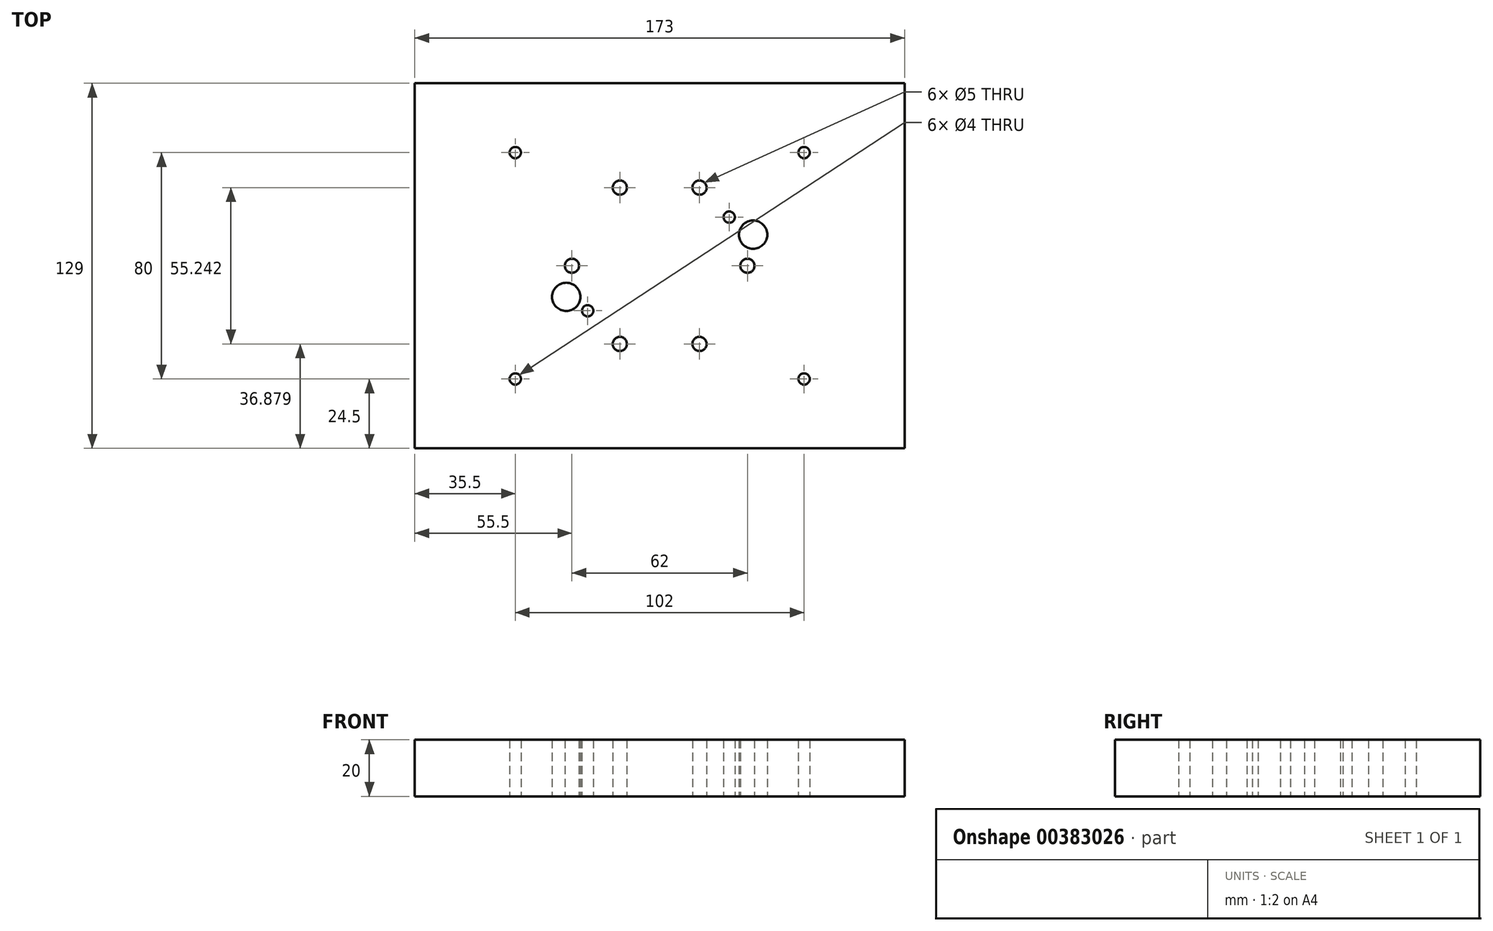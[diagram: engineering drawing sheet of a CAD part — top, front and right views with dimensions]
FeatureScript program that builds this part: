
annotation { "Feature Type Name" : "Feature", "Feature Type Description" : "" }
export const myFeature = defineFeature(function(context is Context, id is Id, definition is map)
    precondition{}
    {
        {
            var Q0;
            Q0=qCreatedBy(makeId("Top.planeOp"),FACE);
            var sketch = newSketch(context, id + "F0", { "sketchPlane" : qUnion([Q0])});
            skCircle(sketch, "E0", {"center": v(31, 0) * mm, "radius": 2.5 * mm});
            skCircle(sketch, "E1.1.0", {"center": v(14.07, 27.62) * mm, "radius": 2.5 * mm});
            skCircle(sketch, "E1.2.0", {"center": v(-14.07, 27.62) * mm, "radius": 2.5 * mm});
            skCircle(sketch, "E1.3.0", {"center": v(-31, 0) * mm, "radius": 2.5 * mm});
            skCircle(sketch, "E1.4.0", {"center": v(-14.07, -27.62) * mm, "radius": 2.5 * mm});
            skCircle(sketch, "E1.5.0", {"center": v(14.07, -27.62) * mm, "radius": 2.5 * mm});
            skPoint(sketch, "E1.center", {"position": v(0, 0) * mm});
            skLineSegment(sketch, "E2.bottom", {"start": v(-56, 45) * mm, "end": v(56, 45) * mm});
            skLineSegment(sketch, "E2.top", {"start": v(-56, -45) * mm, "end": v(56, -45) * mm});
            skLineSegment(sketch, "E2.left", {"start": v(-56, 45) * mm, "end": v(-56, -45) * mm});
            skLineSegment(sketch, "E2.right", {"start": v(56, 45) * mm, "end": v(56, -45) * mm});
            skLineSegment(sketch, "E3", {"start": v(-37.37, 11) * mm, "end": v(33, 11) * mm, "construction": true});
            skLineSegment(sketch, "E4", {"start": v(33, 11) * mm, "end": v(33, -11) * mm, "construction": true});
            skLineSegment(sketch, "E5", {"start": v(33, -11) * mm, "end": v(-33, -11) * mm, "construction": true});
            skLineSegment(sketch, "E6", {"start": v(-33, -11) * mm, "end": v(-33, 11) * mm, "construction": true});
            skCircle(sketch, "E7", {"center": v(-33, 11) * mm, "radius": 5 * mm, "construction": true});
            skCircle(sketch, "E8", {"center": v(33, 11) * mm, "radius": 5 * mm});
            skCircle(sketch, "E9", {"center": v(33, -11) * mm, "radius": 5 * mm, "construction": true});
            skCircle(sketch, "E10", {"center": v(-33, -11) * mm, "radius": 5 * mm});
            skLineSegment(sketch, "E11.bottom", {"start": v(-51, 40) * mm, "end": v(51, 40) * mm, "construction": true});
            skLineSegment(sketch, "E11.top", {"start": v(-51, -40) * mm, "end": v(51, -40) * mm, "construction": true});
            skLineSegment(sketch, "E11.left", {"start": v(-51, 40) * mm, "end": v(-51, -40) * mm, "construction": true});
            skLineSegment(sketch, "E11.right", {"start": v(51, 40) * mm, "end": v(51, -40) * mm, "construction": true});
            skCircle(sketch, "E12", {"center": v(-51, 40) * mm, "radius": 2 * mm});
            skCircle(sketch, "E13", {"center": v(51, 40) * mm, "radius": 2 * mm});
            skCircle(sketch, "E14", {"center": v(51, -40) * mm, "radius": 2 * mm});
            skCircle(sketch, "E15", {"center": v(-51, -40) * mm, "radius": 2 * mm});
            skLineSegment(sketch, "E16", {"start": v(-14.07, -27.62) * mm, "end": v(14.07, 27.62) * mm, "construction": true});
            skLineSegment(sketch, "E17", {"start": v(14.07, -27.62) * mm, "end": v(-14.07, 27.62) * mm, "construction": true});
            skLineSegment(sketch, "E18", {"start": v(55.41, 17.21) * mm, "end": v(-51.67, 17.2) * mm, "construction": true});
            skLineSegment(sketch, "E19", {"start": v(24.57, -95.5) * mm, "end": v(24.57, 92.97) * mm, "construction": true});
            skCircle(sketch, "E20", {"center": v(24.57, 17.21) * mm, "radius": 2 * mm});
            skCircle(sketch, "E21", {"center": v(-25.44, -15.9) * mm, "radius": 2 * mm});
            skSolve(sketch);
        }
        {
            var Q0;
            Q0=qSketchRegion(id+"F0",true);
            extrude(context, id + "F1", {"entities" : qUnion([Q0]), "depth" : 20 * mm, "offsetDistance" : 25 * mm});
        }
        {
            var Q0;
            Q0=makeQuery(id+"F1.opExtrude","CAP_FACE",FACE,{"disambiguationData":[OSD([sQuery(id+"F0.wireOp",EDGE,"E0"),sQuery(id+"F0.wireOp",EDGE,"E1.1.0"),sQuery(id+"F0.wireOp",EDGE,"E1.2.0"),sQuery(id+"F0.wireOp",EDGE,"E1.3.0"),sQuery(id+"F0.wireOp",EDGE,"E1.4.0"),sQuery(id+"F0.wireOp",EDGE,"E1.5.0"),sQuery(id+"F0.wireOp",EDGE,"E2.bottom"),sQuery(id+"F0.wireOp",EDGE,"E2.top"),sQuery(id+"F0.wireOp",EDGE,"E2.left"),sQuery(id+"F0.wireOp",EDGE,"E2.right"),sQuery(id+"F0.wireOp",EDGE,"E8"),sQuery(id+"F0.wireOp",EDGE,"E10"),sQuery(id+"F0.wireOp",EDGE,"E12"),sQuery(id+"F0.wireOp",EDGE,"E13"),sQuery(id+"F0.wireOp",EDGE,"E14"),sQuery(id+"F0.wireOp",EDGE,"E15"),sQuery(id+"F0.wireOp",EDGE,"E20"),sQuery(id+"F0.wireOp",EDGE,"E21")])],"isStart":false});
            var sketch = newSketch(context, id + "F2", { "sketchPlane" : qUnion([Q0])});
            skLineSegment(sketch, "E22.bottom", {"start": v(-86.5, 64.5) * mm, "end": v(86.5, 64.5) * mm});
            skLineSegment(sketch, "E22.top", {"start": v(-86.5, -64.5) * mm, "end": v(86.5, -64.5) * mm});
            skLineSegment(sketch, "E22.left", {"start": v(-86.5, 64.5) * mm, "end": v(-86.5, -64.5) * mm});
            skLineSegment(sketch, "E22.right", {"start": v(86.5, 64.5) * mm, "end": v(86.5, -64.5) * mm});
            skLineSegment(sketch, "E23.0", {"start": v(-56, 45) * mm, "end": v(56, 45) * mm});
            skLineSegment(sketch, "E24.0", {"start": v(56, 45) * mm, "end": v(56, -45) * mm});
            skLineSegment(sketch, "E25.0", {"start": v(-56, -45) * mm, "end": v(56, -45) * mm});
            skLineSegment(sketch, "E26.0", {"start": v(-56, 45) * mm, "end": v(-56, -45) * mm});
            skSolve(sketch);
        }
        {
            var Q0;
            Q0 = qSketchRegion(id + "F2", true);
            var Q1;
            Q1=makeQuery(id+"F1.opExtrude","CAP_FACE",FACE,{"disambiguationData":[OSD([sQuery(id+"F0.wireOp",EDGE,"E0"),sQuery(id+"F0.wireOp",EDGE,"E1.1.0"),sQuery(id+"F0.wireOp",EDGE,"E1.2.0"),sQuery(id+"F0.wireOp",EDGE,"E1.3.0"),sQuery(id+"F0.wireOp",EDGE,"E1.4.0"),sQuery(id+"F0.wireOp",EDGE,"E1.5.0"),sQuery(id+"F0.wireOp",EDGE,"E2.bottom"),sQuery(id+"F0.wireOp",EDGE,"E2.top"),sQuery(id+"F0.wireOp",EDGE,"E2.left"),sQuery(id+"F0.wireOp",EDGE,"E2.right"),sQuery(id+"F0.wireOp",EDGE,"E8"),sQuery(id+"F0.wireOp",EDGE,"E10"),sQuery(id+"F0.wireOp",EDGE,"E12"),sQuery(id+"F0.wireOp",EDGE,"E13"),sQuery(id+"F0.wireOp",EDGE,"E14"),sQuery(id+"F0.wireOp",EDGE,"E15"),sQuery(id+"F0.wireOp",EDGE,"E20"),sQuery(id+"F0.wireOp",EDGE,"E21")])],"isStart":true});
            extrude(context, id + "F3", {"entities" : qUnion([Q0]), "operationType" : NewBodyOperationType.ADD, "endBound" : BoundingType.UP_TO_SURFACE, "oppositeDirection" : true, "depth" : 25 * mm, "endBoundEntityFace" : qUnion([Q1]), "offsetDistance" : 25 * mm});
        }
    });
